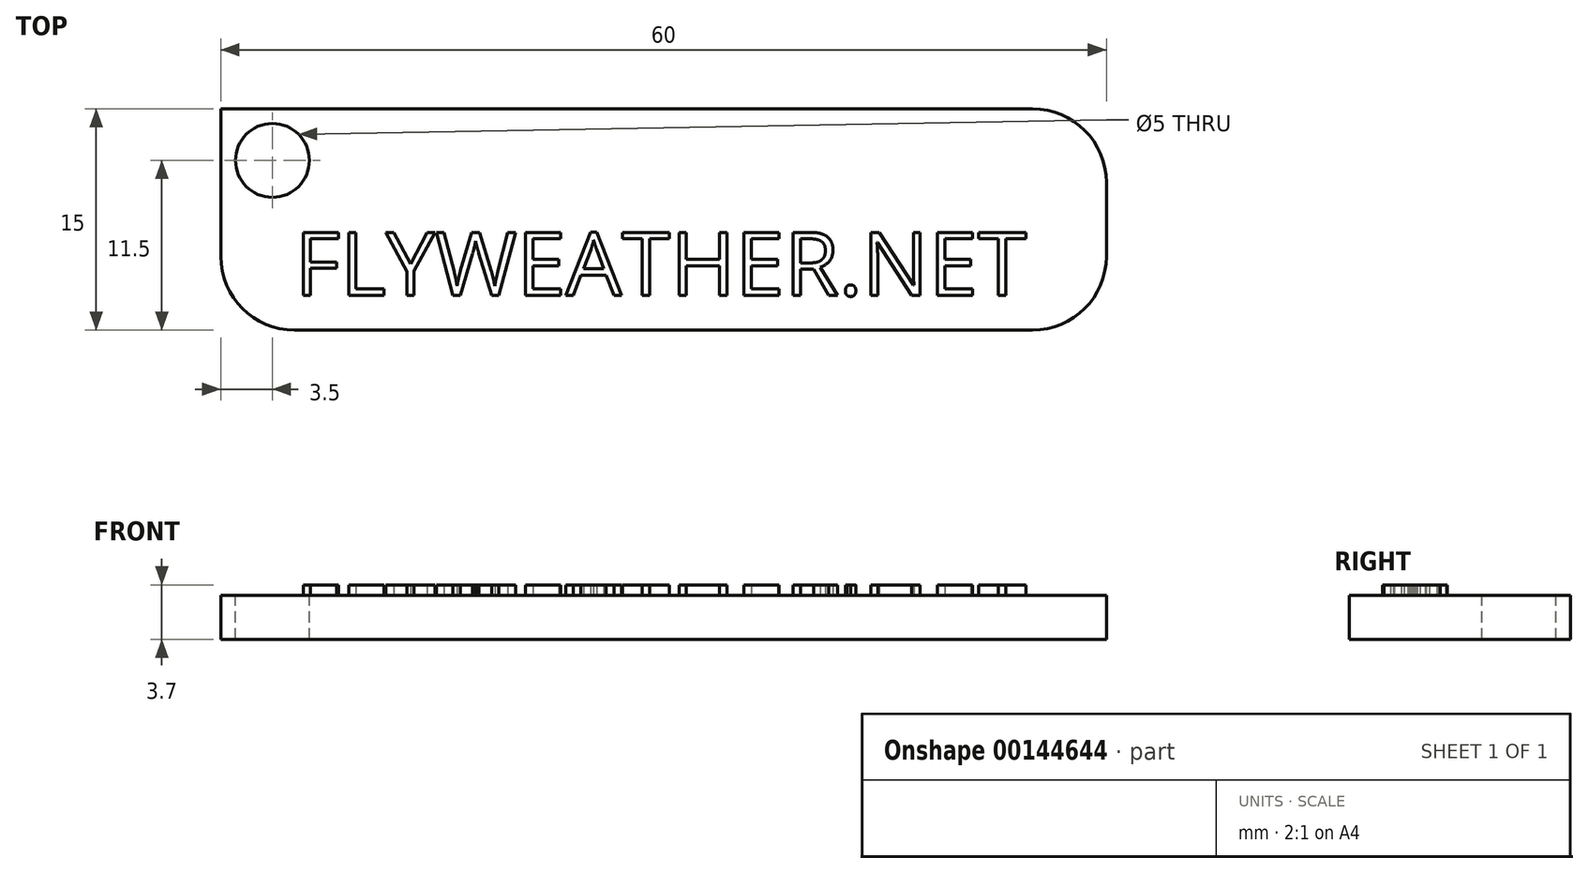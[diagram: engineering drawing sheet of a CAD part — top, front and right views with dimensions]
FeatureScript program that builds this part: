
annotation { "Feature Type Name" : "Feature", "Feature Type Description" : "" }
export const myFeature = defineFeature(function(context is Context, id is Id, definition is map)
    precondition{}
    {
        {
            var Q0;
            Q0=qCreatedBy(makeId("Top.planeOp"),FACE);
            var sketch = newSketch(context, id + "F0", { "sketchPlane" : qUnion([Q0])});
            skLineSegment(sketch, "E0.bottom", {"start": v(0, 0) * mm, "end": v(60, 0) * mm});
            skLineSegment(sketch, "E0.top", {"start": v(0, -15) * mm, "end": v(60, -15) * mm});
            skLineSegment(sketch, "E0.left", {"start": v(0, 0) * mm, "end": v(0, -15) * mm});
            skLineSegment(sketch, "E0.right", {"start": v(60, 0) * mm, "end": v(60, -15) * mm});
            skSolve(sketch);
        }
        {
            var Q0;
            Q0=makeQuery(id+"F0.imprint","IMPRINT",FACE,{"disambiguationData":[TD([[makeQuery(id+"F0.imprint","IMPRINT",EDGE,{"derivedFrom":sQuery(id+"F0.wireOp",EDGE,"E0.bottom")}),-1.0]])]});
            extrude(context, id + "F1", {"entities" : qUnion([Q0]), "depth" : 3 * mm});
        }
        {
            var Q0;
            Q0=makeQuery(id+"F1.opExtrude","SWEPT_EDGE",EDGE,{"disambiguationData":[OSD([sQuery(id+"F0.wireOp",EDGE,"E0.top"),sQuery(id+"F0.wireOp",EDGE,"E0.right")])]});
            var Q1;
            Q1=makeQuery(id+"F1.opExtrude","SWEPT_EDGE",EDGE,{"disambiguationData":[OSD([sQuery(id+"F0.wireOp",EDGE,"E0.bottom"),sQuery(id+"F0.wireOp",EDGE,"E0.right")])]});
            var Q2;
            Q2=makeQuery(id+"F1.opExtrude","SWEPT_EDGE",EDGE,{"disambiguationData":[OSD([sQuery(id+"F0.wireOp",EDGE,"E0.top"),sQuery(id+"F0.wireOp",EDGE,"E0.left")])]});
            fillet(context, id + "F2", {"entities" : qUnion([Q0, Q1, Q2]), "radius" : 5 * mm, "tangentPropagation" : true, "allowEdgeOverflow" : false});
        }
        {
            var Q0;
            Q0=makeQuery(id+"F1.opExtrude","CAP_FACE",FACE,{"disambiguationData":[OSD([sQuery(id+"F0.wireOp",EDGE,"E0.bottom"),sQuery(id+"F0.wireOp",EDGE,"E0.top"),sQuery(id+"F0.wireOp",EDGE,"E0.left"),sQuery(id+"F0.wireOp",EDGE,"E0.right")])],"isStart":false});
            var sketch = newSketch(context, id + "F3", { "sketchPlane" : qUnion([Q0])});
            skCircle(sketch, "E1", {"center": v(3.5, -3.5) * mm, "radius": 2.5 * mm});
            skPoint(sketch, "E1.first.point", {"position": v(1.65, -1.82) * mm});
            skPoint(sketch, "E1.second.point", {"position": v(4.94, -5.55) * mm});
            skPoint(sketch, "E1.third.point", {"position": v(4.73, -1.32) * mm});
            skSolve(sketch);
        }
        {
            var Q0;
            Q0 = qSketchRegion(id + "F3", true);
            extrude(context, id + "F4", {"entities" : qUnion([Q0]), "operationType" : NewBodyOperationType.REMOVE, "oppositeDirection" : true, "depth" : 25 * mm});
        }
        {
            var Q0;
            Q0=makeQuery(id+"F1.opExtrude","CAP_FACE",FACE,{"disambiguationData":[OSD([sQuery(id+"F0.wireOp",EDGE,"E0.bottom"),sQuery(id+"F0.wireOp",EDGE,"E0.top"),sQuery(id+"F0.wireOp",EDGE,"E0.left"),sQuery(id+"F0.wireOp",EDGE,"E0.right")])],"isStart":false});
            var sketch = newSketch(context, id + "F5", { "sketchPlane" : qUnion([Q0])});
            skText(sketch, "E2", { "text": "FLYWEATHER.NET", "fontName": "OpenSans-Regular.ttf"});
            const initialGuessF5  = {"E2": [0.005, -0.01264, 1, 0, 0.0043]};
            skSetInitialGuess(sketch, initialGuessF5);
            skSolve(sketch);
        }
        {
            var Q0;
            Q0 = qSketchRegion(id + "F5", true);
            extrude(context, id + "F6", {"entities" : qUnion([Q0]), "operationType" : NewBodyOperationType.ADD, "depth" : 0.7 * mm});
        }
    });
